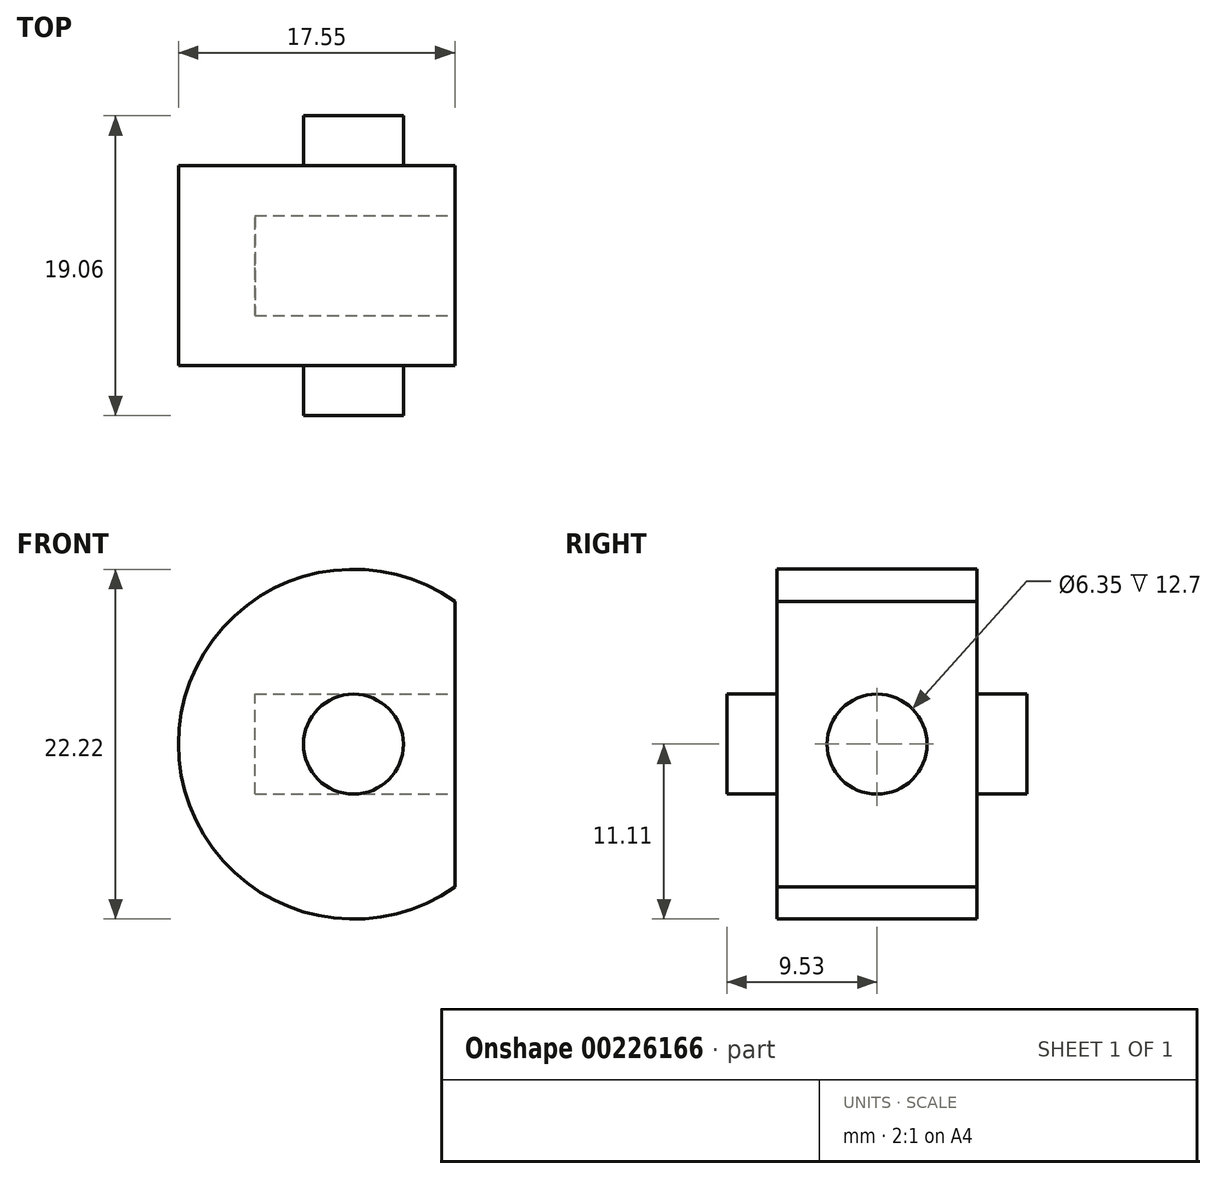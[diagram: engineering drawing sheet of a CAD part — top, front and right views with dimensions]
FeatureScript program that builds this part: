
annotation { "Feature Type Name" : "Feature", "Feature Type Description" : "" }
export const myFeature = defineFeature(function(context is Context, id is Id, definition is map)
    precondition{}
    {
        {
            var Q0;
            Q0=qCreatedBy(makeId("Front.planeOp"),FACE);
            var sketch = newSketch(context, id + "F0", { "sketchPlane" : qUnion([Q0])});
            skCircle(sketch, "E0", {"center": v(0, 0) * mm, "radius": 11.11 * mm});
            skSolve(sketch);
        }
        {
            var Q0;
            Q0 = qSketchRegion(id + "F0", true);
            extrude(context, id + "F1", {"entities" : qUnion([Q0]), "endBound" : BoundingType.SYMMETRIC, "depth" : 12.7 * mm});
        }
        {
            var Q0;
            Q0=makeQuery(id+"F1.opExtrude","CAP_FACE",FACE,{"disambiguationData":[OSD([sQuery(id+"F0.wireOp",EDGE,"E0")])],"isStart":false});
            var sketch = newSketch(context, id + "F2", { "sketchPlane" : qUnion([Q0])});
            skCircle(sketch, "E1", {"center": v(0, 0) * mm, "radius": 3.18 * mm});
            skSolve(sketch);
        }
        {
            var Q0;
            Q0 = qSketchRegion(id + "F2", true);
            extrude(context, id + "F3", {"entities" : qUnion([Q0]), "operationType" : NewBodyOperationType.ADD, "depth" : 3.17 * mm});
        }
        {
            var Q0;
            Q0=makeQuery(id+"F1.opExtrude","CAP_FACE",FACE,{"disambiguationData":[OSD([sQuery(id+"F0.wireOp",EDGE,"E0")])],"isStart":true});
            var sketch = newSketch(context, id + "F4", { "sketchPlane" : qUnion([Q0])});
            skCircle(sketch, "E2", {"center": v(0, 0) * mm, "radius": 3.18 * mm});
            skSolve(sketch);
        }
        {
            var Q0;
            Q0 = qSketchRegion(id + "F4", true);
            extrude(context, id + "F5", {"entities" : qUnion([Q0]), "operationType" : NewBodyOperationType.ADD, "depth" : 3.17 * mm});
        }
        {
            var Q0;
            Q0=makeQuery(id+"F5.opExtrude","CAP_FACE",FACE,{"disambiguationData":[OSD([sQuery(id+"F4.wireOp",EDGE,"E2")])],"isStart":false});
            var sketch = newSketch(context, id + "F6", { "sketchPlane" : qUnion([Q0])});
            skLineSegment(sketch, "E3.right", {"start": v(-6.44, -10.16) * mm, "end": v(-6.44, 9.06) * mm});
            skPoint(sketch, "E3.middle", {"position": v(0, 0) * mm});
            skArc(sketch, "E4", {"start": v(-6.44, 9.06) * mm, "mid": v(1.11, -11.06) * mm, "end": v(4.5, 10.16) * mm});
            skPoint(sketch, "E5.orphan", {"position": v(-6.44, 10.16) * mm});
            skPoint(sketch, "E6.orphan", {"position": v(6.44, 10.16) * mm});
            skPoint(sketch, "E3.left.start.orphan", {"position": v(6.44, -10.16) * mm});
            skSolve(sketch);
        }
        {
            var Q0;
            Q0 = qSketchRegion(id + "F6", true);
            extrude(context, id + "F7", {"entities" : qUnion([Q0]), "operationType" : NewBodyOperationType.REMOVE, "oppositeDirection" : true, "depth" : 25.4 * mm});
        }
        {
            var Q0;
            Q0=makeQuery(id+"F7.boolean.opBoolean","COPY",FACE,{"derivedFrom":makeQuery(id+"F7.opExtrude","SWEPT_FACE",FACE,{"disambiguationData":[OSD([sQuery(id+"F6.wireOp",EDGE,"E3.right")])]})});
            var sketch = newSketch(context, id + "F8", { "sketchPlane" : qUnion([Q0])});
            skCircle(sketch, "E7", {"center": v(0, 0) * mm, "radius": 3.18 * mm});
            skSolve(sketch);
        }
        {
            var Q0;
            Q0 = qSketchRegion(id + "F8", true);
            extrude(context, id + "F9", {"entities" : qUnion([Q0]), "operationType" : NewBodyOperationType.REMOVE, "oppositeDirection" : true, "depth" : 12.7 * mm});
        }
    });
